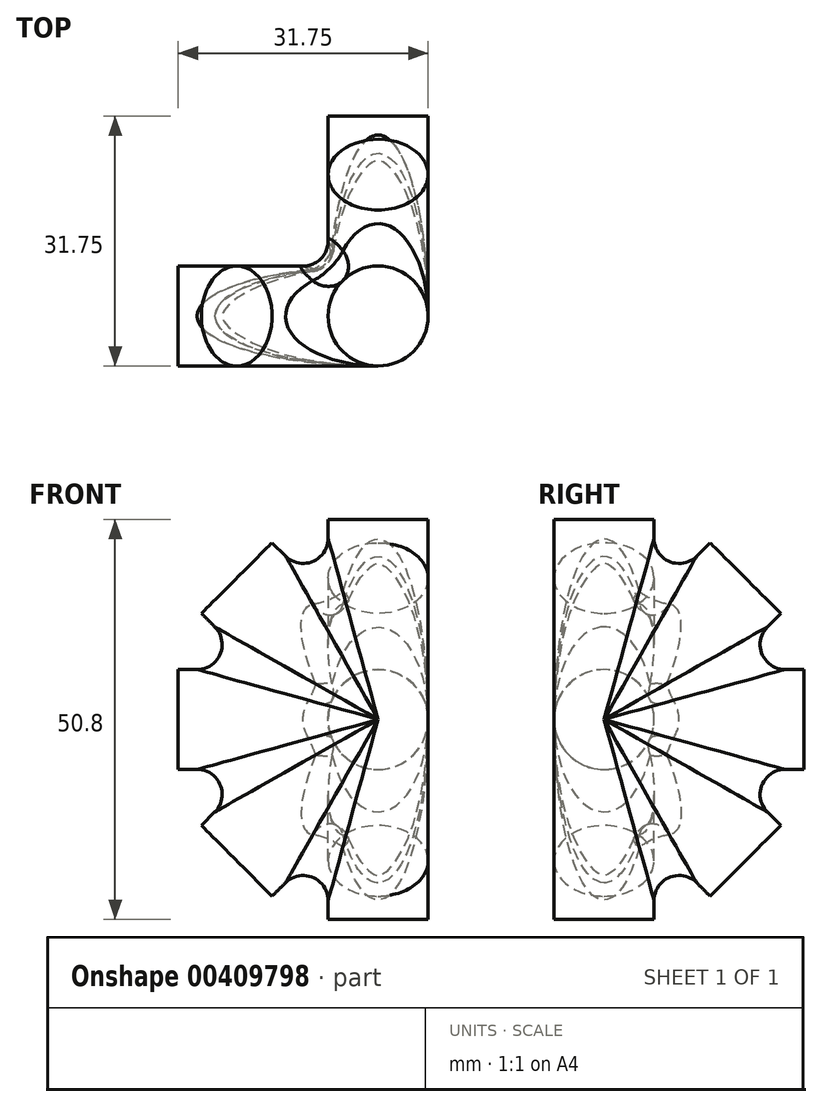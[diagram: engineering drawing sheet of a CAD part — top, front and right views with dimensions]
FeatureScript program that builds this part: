
annotation { "Feature Type Name" : "Feature", "Feature Type Description" : "" }
export const myFeature = defineFeature(function(context is Context, id is Id, definition is map)
    precondition{}
    {
        {
            var Q0;
            Q0=qCreatedBy(makeId("Top.planeOp"),FACE);
            var sketch = newSketch(context, id + "F0", { "sketchPlane" : qUnion([Q0])});
            skCircle(sketch, "E0", {"center": v(0, 0) * mm, "radius": 6.35 * mm});
            skSolve(sketch);
        }
        {
            var Q0;
            Q0 = qSketchRegion(id + "F0", true);
            extrude(context, id + "F1", {"entities" : qUnion([Q0]), "depth" : 50.8 * mm, "symmetric" : true});
        }
        {
            var Q0;
            Q0=qCreatedBy(makeId("Right.planeOp"),FACE);
            var sketch = newSketch(context, id + "F2", { "sketchPlane" : qUnion([Q0])});
            skCircle(sketch, "E1", {"center": v(0, 0) * mm, "radius": 6.35 * mm});
            skSolve(sketch);
        }
        {
            var Q0;
            Q0 = qSketchRegion(id + "F2", true);
            extrude(context, id + "F3", {"entities" : qUnion([Q0]), "operationType" : NewBodyOperationType.ADD, "oppositeDirection" : true, "depth" : 25.4 * mm});
        }
        {
            var Q0;
            Q0=qCreatedBy(makeId("Front.planeOp"),FACE);
            var sketch = newSketch(context, id + "F4", { "sketchPlane" : qUnion([Q0])});
            skCircle(sketch, "E2", {"center": v(0, 0) * mm, "radius": 6.35 * mm});
            skSolve(sketch);
        }
        {
            var Q0;
            Q0 = qSketchRegion(id + "F4", true);
            extrude(context, id + "F5", {"entities" : qUnion([Q0]), "operationType" : NewBodyOperationType.ADD, "oppositeDirection" : true, "depth" : 25.4 * mm});
        }
        {
            var Q0;
            Q0=qCreatedBy(makeId("Top.planeOp"),FACE);
            var sketch = newSketch(context, id + "F6", { "sketchPlane" : qUnion([Q0])});
            skLineSegment(sketch, "E3", {"start": v(0, 0) * mm, "end": v(0, 25.4) * mm});
            skLineSegment(sketch, "E4", {"start": v(0, 0) * mm, "end": v(-25.4, 0) * mm});
            skSolve(sketch);
        }
        {
            var Q0;
            Q0=sQuery(id+"F6.wireOp",EDGE,"E4");
            cPlane(context, id + "F7", {"entities" : qUnion([Q0]), "cplaneType" : CPlaneType.LINE_ANGLE, "offset" : 25.4 * mm, "angle" : 45 * degree, "width" : 152.4 * mm, "height" : 152.4 * mm});
        }
        {
            var Q0;
            Q0=sQuery(id+"F6.wireOp",EDGE,"E4");
            cPlane(context, id + "F8", {"entities" : qUnion([Q0]), "cplaneType" : CPlaneType.LINE_ANGLE, "offset" : 25.4 * mm, "angle" : 135 * degree, "width" : 152.4 * mm, "height" : 152.4 * mm});
        }
        {
            var Q0;
            Q0=sQuery(id+"F6.wireOp",EDGE,"E3");
            cPlane(context, id + "F9", {"entities" : qUnion([Q0]), "cplaneType" : CPlaneType.LINE_ANGLE, "offset" : 25.4 * mm, "angle" : 45 * degree, "width" : 152.4 * mm, "height" : 152.4 * mm});
        }
        {
            var Q0;
            Q0=sQuery(id+"F6.wireOp",EDGE,"E3");
            cPlane(context, id + "F10", {"entities" : qUnion([Q0]), "cplaneType" : CPlaneType.LINE_ANGLE, "offset" : 25.4 * mm, "angle" : 135 * degree, "width" : 152.4 * mm, "height" : 152.4 * mm});
        }
        {
            var Q0;
            Q0=qCreatedBy(id+"F7.planeOp",FACE);
            var sketch = newSketch(context, id + "F11", { "sketchPlane" : qUnion([Q0])});
            skCircle(sketch, "E5", {"center": v(0, 0) * mm, "radius": 6.35 * mm});
            skSolve(sketch);
        }
        {
            var Q0;
            Q0 = qSketchRegion(id + "F11", true);
            extrude(context, id + "F12", {"entities" : qUnion([Q0]), "operationType" : NewBodyOperationType.ADD, "oppositeDirection" : true, "depth" : 25.4 * mm});
        }
        {
            var Q0;
            Q0=qCreatedBy(id+"F8.planeOp",FACE);
            var sketch = newSketch(context, id + "F13", { "sketchPlane" : qUnion([Q0])});
            skCircle(sketch, "E6", {"center": v(0, 0) * mm, "radius": 6.35 * mm});
            skSolve(sketch);
        }
        {
            var Q0;
            Q0 = qSketchRegion(id + "F13", true);
            extrude(context, id + "F14", {"entities" : qUnion([Q0]), "operationType" : NewBodyOperationType.ADD, "depth" : 25.4 * mm});
        }
        {
            var Q0;
            Q0=qCreatedBy(id+"F9.planeOp",FACE);
            var sketch = newSketch(context, id + "F15", { "sketchPlane" : qUnion([Q0])});
            skCircle(sketch, "E7", {"center": v(0, 0) * mm, "radius": 6.35 * mm});
            skSolve(sketch);
        }
        {
            var Q0;
            Q0 = qSketchRegion(id + "F15", true);
            extrude(context, id + "F16", {"entities" : qUnion([Q0]), "operationType" : NewBodyOperationType.ADD, "oppositeDirection" : true, "depth" : 25.4 * mm});
        }
        {
            var Q0;
            Q0=qCreatedBy(id+"F10.planeOp",FACE);
            var sketch = newSketch(context, id + "F17", { "sketchPlane" : qUnion([Q0])});
            skCircle(sketch, "E8", {"center": v(0, 0) * mm, "radius": 6.35 * mm});
            skSolve(sketch);
        }
        {
            var Q0;
            Q0 = qSketchRegion(id + "F17", true);
            extrude(context, id + "F18", {"entities" : qUnion([Q0]), "operationType" : NewBodyOperationType.ADD, "oppositeDirection" : true, "depth" : 25.4 * mm});
        }
        {
            var Q0;
            Q0=makeQuery(id+"F14.boolean.opBoolean","INTERSECT",EDGE,{"derivedFrom":[makeQuery(id+"F5.opExtrude","SWEPT_FACE",FACE,{"disambiguationData":[OSD([sQuery(id+"F4.wireOp",EDGE,"E2")])]}),makeQuery(id+"F14.opExtrude","SWEPT_FACE",FACE,{"disambiguationData":[OSD([sQuery(id+"F13.wireOp",EDGE,"E6")])]})]});
            var Q1;
            Q1=makeQuery(id+"F12.boolean.opBoolean","INTERSECT",EDGE,{"derivedFrom":[makeQuery(id+"F5.opExtrude","SWEPT_FACE",FACE,{"disambiguationData":[OSD([sQuery(id+"F4.wireOp",EDGE,"E2")])]}),makeQuery(id+"F12.opExtrude","SWEPT_FACE",FACE,{"disambiguationData":[OSD([sQuery(id+"F11.wireOp",EDGE,"E5")])]})]});
            var Q2;
            Q2=makeQuery(id+"F16.boolean.opBoolean","INTERSECT",EDGE,{"derivedFrom":[makeQuery(id+"F3.opExtrude","SWEPT_FACE",FACE,{"disambiguationData":[OSD([sQuery(id+"F2.wireOp",EDGE,"E1")])]}),makeQuery(id+"F16.opExtrude","SWEPT_FACE",FACE,{"disambiguationData":[OSD([sQuery(id+"F15.wireOp",EDGE,"E7")])]})]});
            var Q3;
            Q3=makeQuery(id+"F18.boolean.opBoolean","INTERSECT",EDGE,{"derivedFrom":[makeQuery(id+"F3.opExtrude","SWEPT_FACE",FACE,{"disambiguationData":[OSD([sQuery(id+"F2.wireOp",EDGE,"E1")])]}),makeQuery(id+"F18.opExtrude","SWEPT_FACE",FACE,{"disambiguationData":[OSD([sQuery(id+"F17.wireOp",EDGE,"E8")])]})]});
            fillet(context, id + "F19", {"entities" : qUnion([Q0, Q1, Q2, Q3]), "radius" : 3.17 * mm, "tangentPropagation" : true, "allowEdgeOverflow" : false});
        }
        {
            var Q0;
            Q0=makeQuery(id+"F18.boolean.opBoolean","INTERSECT",EDGE,{"derivedFrom":[makeQuery(id+"F14.opExtrude","SWEPT_FACE",FACE,{"disambiguationData":[OSD([sQuery(id+"F13.wireOp",EDGE,"E6")])]}),makeQuery(id+"F18.opExtrude","SWEPT_FACE",FACE,{"disambiguationData":[OSD([sQuery(id+"F17.wireOp",EDGE,"E8")])]})]});
            var Q1;
            Q1=makeQuery(id+"F18.boolean.opBoolean","INTERSECT",EDGE,{"derivedFrom":[makeQuery(id+"F1.opExtrude","SWEPT_FACE",FACE,{"disambiguationData":[OSD([sQuery(id+"F0.wireOp",EDGE,"E0")])]}),makeQuery(id+"F18.opExtrude","SWEPT_FACE",FACE,{"disambiguationData":[OSD([sQuery(id+"F17.wireOp",EDGE,"E8")])]})]});
            var Q2;
            Q2=makeQuery(id+"F16.boolean.opBoolean","INTERSECT",EDGE,{"derivedFrom":[makeQuery(id+"F1.opExtrude","SWEPT_FACE",FACE,{"disambiguationData":[OSD([sQuery(id+"F0.wireOp",EDGE,"E0")])]}),makeQuery(id+"F16.opExtrude","SWEPT_FACE",FACE,{"disambiguationData":[OSD([sQuery(id+"F15.wireOp",EDGE,"E7")])]})]});
            var Q3;
            Q3=makeQuery(id+"F14.boolean.opBoolean","INTERSECT",EDGE,{"derivedFrom":[makeQuery(id+"F1.opExtrude","SWEPT_FACE",FACE,{"disambiguationData":[OSD([sQuery(id+"F0.wireOp",EDGE,"E0")])]}),makeQuery(id+"F14.opExtrude","SWEPT_FACE",FACE,{"disambiguationData":[OSD([sQuery(id+"F13.wireOp",EDGE,"E6")])]})]});
            var Q4;
            Q4=makeQuery(id+"F12.boolean.opBoolean","INTERSECT",EDGE,{"derivedFrom":[makeQuery(id+"F1.opExtrude","SWEPT_FACE",FACE,{"disambiguationData":[OSD([sQuery(id+"F0.wireOp",EDGE,"E0")])]}),makeQuery(id+"F12.opExtrude","SWEPT_FACE",FACE,{"disambiguationData":[OSD([sQuery(id+"F11.wireOp",EDGE,"E5")])]})]});
            fillet(context, id + "F20", {"entities" : qUnion([Q0, Q1, Q2, Q3, Q4]), "radius" : 3.17 * mm, "tangentPropagation" : true, "allowEdgeOverflow" : false});
        }
    });
